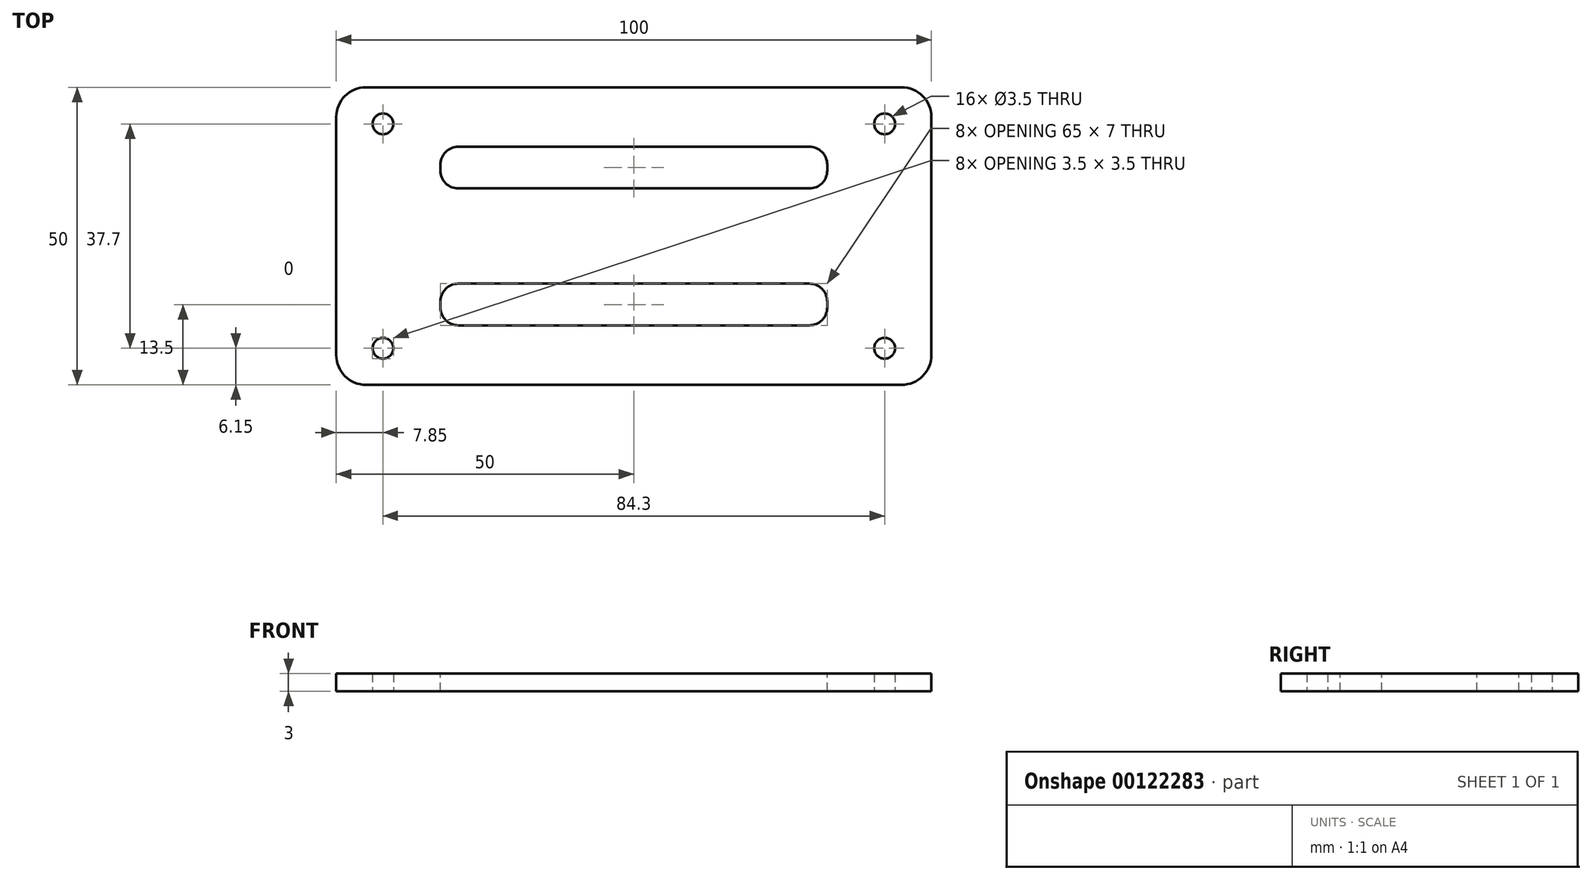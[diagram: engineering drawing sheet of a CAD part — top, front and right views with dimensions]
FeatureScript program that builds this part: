
annotation { "Feature Type Name" : "Feature", "Feature Type Description" : "" }
export const myFeature = defineFeature(function(context is Context, id is Id, definition is map)
    precondition{}
    {
        {
            var Q0;
            Q0=qCreatedBy(makeId("Top.planeOp"),FACE);
            var sketch = newSketch(context, id + "F0", { "sketchPlane" : qUnion([Q0])});
            skLineSegment(sketch, "E0.bottom", {"start": v(-50, 25) * mm, "end": v(50, 25) * mm});
            skLineSegment(sketch, "E0.top", {"start": v(-50, -25) * mm, "end": v(50, -25) * mm});
            skLineSegment(sketch, "E0.left", {"start": v(-50, 25) * mm, "end": v(-50, -25) * mm});
            skLineSegment(sketch, "E0.right", {"start": v(50, 25) * mm, "end": v(50, -25) * mm});
            skPoint(sketch, "E0.middle", {"position": v(0, 0) * mm});
            skLineSegment(sketch, "E1.bottom", {"start": v(-42.15, 18.85) * mm, "end": v(42.15, 18.85) * mm, "construction": true});
            skLineSegment(sketch, "E1.top", {"start": v(-42.15, -18.85) * mm, "end": v(42.15, -18.85) * mm, "construction": true});
            skLineSegment(sketch, "E1.left", {"start": v(-42.15, 18.85) * mm, "end": v(-42.15, -18.85) * mm, "construction": true});
            skLineSegment(sketch, "E1.right", {"start": v(42.15, 18.85) * mm, "end": v(42.15, -18.85) * mm, "construction": true});
            skSolve(sketch);
        }
        {
            var Q0;
            Q0=makeQuery(id+"F0.imprint","IMPRINT",FACE,{"disambiguationData":[TD([[makeQuery(id+"F0.imprint","IMPRINT",EDGE,{"derivedFrom":sQuery(id+"F0.wireOp",EDGE,"E0.bottom")}),-1.0]])]});
            extrude(context, id + "F1", {"entities" : qUnion([Q0]), "depth" : 3 * mm});
        }
        {
            var Q0;
            Q0=sQuery(id+"F0.wireOp",VERTEX,"E1.left.start");
            var Q1;
            Q1=sQuery(id+"F0.wireOp",VERTEX,"E1.left.end");
            var Q2;
            Q2=sQuery(id+"F0.wireOp",VERTEX,"E1.right.start");
            var Q3;
            Q3=sQuery(id+"F0.wireOp",VERTEX,"E1.right.end");
            var Q4;
            Q4=makeQuery(id+"F1.opExtrude","SWEPT_BODY",BODY,{"disambiguationData":[OSD([sQuery(id+"F0.wireOp",EDGE,"E0.bottom"),sQuery(id+"F0.wireOp",EDGE,"E0.top"),sQuery(id+"F0.wireOp",EDGE,"E0.left"),sQuery(id+"F0.wireOp",EDGE,"E0.right")])]});
            hole(context, id + "F2", {"style" : HoleStyle.SIMPLE, "endStyle" : HoleEndStyle.BLIND, "oppositeDirection" : true, "holeDiameter" : 3.5 * mm, "holeDepth" : 16 * mm, "startFromSketch" : true, "locations" : qUnion([Q0, Q1, Q2, Q3]), "scope" : qUnion([Q4])});
        }
        {
            var Q0;
            Q0=makeQuery(id+"F1.opExtrude","SWEPT_EDGE",EDGE,{"disambiguationData":[OSD([sQuery(id+"F0.wireOp",EDGE,"E0.bottom"),sQuery(id+"F0.wireOp",EDGE,"E0.left")])]});
            var Q1;
            Q1=makeQuery(id+"F1.opExtrude","SWEPT_EDGE",EDGE,{"disambiguationData":[OSD([sQuery(id+"F0.wireOp",EDGE,"E0.top"),sQuery(id+"F0.wireOp",EDGE,"E0.left")])]});
            var Q2;
            Q2=makeQuery(id+"F1.opExtrude","SWEPT_EDGE",EDGE,{"disambiguationData":[OSD([sQuery(id+"F0.wireOp",EDGE,"E0.bottom"),sQuery(id+"F0.wireOp",EDGE,"E0.right")])]});
            var Q3;
            Q3=makeQuery(id+"F1.opExtrude","SWEPT_EDGE",EDGE,{"disambiguationData":[OSD([sQuery(id+"F0.wireOp",EDGE,"E0.top"),sQuery(id+"F0.wireOp",EDGE,"E0.right")])]});
            fillet(context, id + "F3", {"entities" : qUnion([Q0, Q1, Q2, Q3]), "radius" : 5 * mm, "tangentPropagation" : true, "allowEdgeOverflow" : false});
        }
        {
            var Q0;
            Q0=makeQuery(id+"F1.opExtrude","CAP_FACE",FACE,{"disambiguationData":[OSD([sQuery(id+"F0.wireOp",EDGE,"E0.bottom"),sQuery(id+"F0.wireOp",EDGE,"E0.top"),sQuery(id+"F0.wireOp",EDGE,"E0.left"),sQuery(id+"F0.wireOp",EDGE,"E0.right")])],"isStart":false});
            var sketch = newSketch(context, id + "F4", { "sketchPlane" : qUnion([Q0])});
            skLineSegment(sketch, "E2.bottom", {"start": v(-32.5, 15) * mm, "end": v(32.5, 15) * mm});
            skLineSegment(sketch, "E2.top", {"start": v(-32.5, 8) * mm, "end": v(32.5, 8) * mm});
            skLineSegment(sketch, "E2.left", {"start": v(-32.5, 15) * mm, "end": v(-32.5, 8) * mm});
            skLineSegment(sketch, "E2.right", {"start": v(32.5, 15) * mm, "end": v(32.5, 8) * mm});
            skLineSegment(sketch, "E3.MirrorCS", {"start": v(32.5, -15) * mm, "end": v(32.5, -8) * mm});
            skLineSegment(sketch, "E4.MirrorCS", {"start": v(-32.5, -15) * mm, "end": v(32.5, -15) * mm});
            skLineSegment(sketch, "E5.MirrorCS", {"start": v(-32.5, -15) * mm, "end": v(-32.5, -8) * mm});
            skLineSegment(sketch, "E6.MirrorCS", {"start": v(-32.5, -8) * mm, "end": v(32.5, -8) * mm});
            skSolve(sketch);
        }
        {
            var Q0;
            Q0=makeQuery(id+"F4.imprint","IMPRINT",FACE,{"disambiguationData":[TD([[makeQuery(id+"F4.imprint","IMPRINT",EDGE,{"derivedFrom":sQuery(id+"F4.wireOp",EDGE,"E2.bottom")}),-1.0]])]});
            var Q1;
            Q1=makeQuery(id+"F4.imprint","IMPRINT",FACE,{"disambiguationData":[TD([[makeQuery(id+"F4.imprint","IMPRINT",EDGE,{"derivedFrom":sQuery(id+"F4.wireOp",EDGE,"E3.MirrorCS")}),1.0]])]});
            extrude(context, id + "F5", {"entities" : qUnion([Q0, Q1]), "operationType" : NewBodyOperationType.REMOVE, "oppositeDirection" : true, "depth" : 25 * mm});
        }
        {
            var Q0;
            Q0=makeQuery(id+"F5.boolean.opBoolean","COPY",EDGE,{"derivedFrom":makeQuery(id+"F5.opExtrude","SWEPT_EDGE",EDGE,{"disambiguationData":[OSD([sQuery(id+"F4.wireOp",EDGE,"E2.bottom"),sQuery(id+"F4.wireOp",EDGE,"E2.left")])]})});
            var Q1;
            Q1=makeQuery(id+"F5.boolean.opBoolean","COPY",EDGE,{"derivedFrom":makeQuery(id+"F5.opExtrude","SWEPT_EDGE",EDGE,{"disambiguationData":[OSD([sQuery(id+"F4.wireOp",EDGE,"E2.top"),sQuery(id+"F4.wireOp",EDGE,"E2.left")])]})});
            var Q2;
            Q2=makeQuery(id+"F5.boolean.opBoolean","COPY",EDGE,{"derivedFrom":makeQuery(id+"F5.opExtrude","SWEPT_EDGE",EDGE,{"disambiguationData":[OSD([sQuery(id+"F4.wireOp",EDGE,"E4.MirrorCS"),sQuery(id+"F4.wireOp",EDGE,"E5.MirrorCS")])]})});
            var Q3;
            Q3=makeQuery(id+"F5.boolean.opBoolean","COPY",EDGE,{"derivedFrom":makeQuery(id+"F5.opExtrude","SWEPT_EDGE",EDGE,{"disambiguationData":[OSD([sQuery(id+"F4.wireOp",EDGE,"E2.top"),sQuery(id+"F4.wireOp",EDGE,"E2.right")])]})});
            var Q4;
            Q4=makeQuery(id+"F5.boolean.opBoolean","COPY",EDGE,{"derivedFrom":makeQuery(id+"F5.opExtrude","SWEPT_EDGE",EDGE,{"disambiguationData":[OSD([sQuery(id+"F4.wireOp",EDGE,"E3.MirrorCS"),sQuery(id+"F4.wireOp",EDGE,"E4.MirrorCS")])]})});
            var Q5;
            Q5=makeQuery(id+"F5.boolean.opBoolean","COPY",EDGE,{"derivedFrom":makeQuery(id+"F5.opExtrude","SWEPT_EDGE",EDGE,{"disambiguationData":[OSD([sQuery(id+"F4.wireOp",EDGE,"E2.bottom"),sQuery(id+"F4.wireOp",EDGE,"E2.right")])]})});
            var Q6;
            Q6=makeQuery(id+"F5.boolean.opBoolean","COPY",EDGE,{"derivedFrom":makeQuery(id+"F5.opExtrude","SWEPT_EDGE",EDGE,{"disambiguationData":[OSD([sQuery(id+"F4.wireOp",EDGE,"E3.MirrorCS"),sQuery(id+"F4.wireOp",EDGE,"E6.MirrorCS")])]})});
            var Q7;
            Q7=makeQuery(id+"F5.boolean.opBoolean","COPY",EDGE,{"derivedFrom":makeQuery(id+"F5.opExtrude","SWEPT_EDGE",EDGE,{"disambiguationData":[OSD([sQuery(id+"F4.wireOp",EDGE,"E5.MirrorCS"),sQuery(id+"F4.wireOp",EDGE,"E6.MirrorCS")])]})});
            fillet(context, id + "F6", {"entities" : qUnion([Q0, Q1, Q2, Q3, Q4, Q5, Q6, Q7]), "radius" : 3 * mm, "tangentPropagation" : true, "allowEdgeOverflow" : false});
        }
    });
